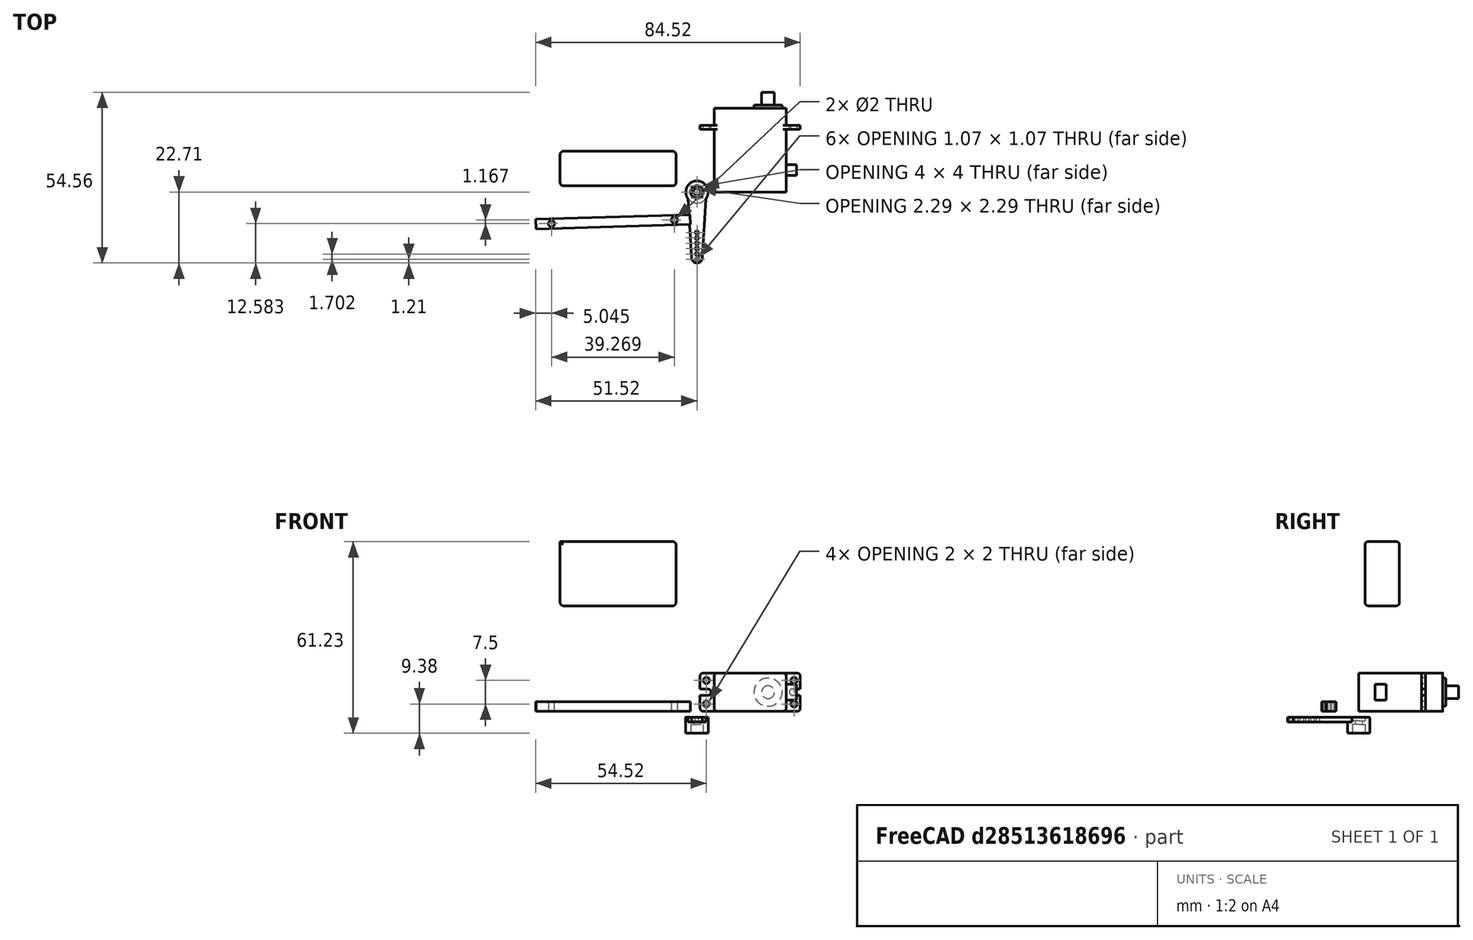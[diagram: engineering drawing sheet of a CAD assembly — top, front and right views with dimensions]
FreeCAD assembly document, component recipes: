
FREECAD ASSEMBLY — COMPONENT RECIPES ("ServoMount")

This assembly document has 3 components, labeled P0..P2 below (a component is one placed body or linked part). 1 of them carries a construction recipe — the FreeCAD feature program that regenerates the part from scratch, quoted from this document or its linked companion documents; the rest are supplied as boundary geometry only. No exploded tour is included for this assembly.
COMPONENT P0 — recipe-attached ("arm", modeled in this document).
Construction recipe (the document's own serialized feature program — sketch geometry with constraints, then the solid features built on it; lengths are millimeters unless a unit is written):

FEATURE [Sketcher::SketchObject] Sketch
  FullyConstrained = false
  MapMode = 5
  Support = -> [XY_Plane003]
  sketch-geometry (8):
    g0: LineSegment StartX=-56.9257 StartY=-11.8541 StartZ=0 EndX=-57.0196 EndY=-8.6971 EndZ=0
    g1: LineSegment StartX=-57.0196 StartY=-8.6971 StartZ=0 EndX=-7.75492 EndY=-7.23288 EndZ=0
    g2: LineSegment StartX=-7.75492 StartY=-7.23288 StartZ=0 EndX=-7.66109 EndY=-10.3899 EndZ=0
    g3: LineSegment StartX=-7.66109 StartY=-10.3899 StartZ=0 EndX=-56.9257 EndY=-11.8541 EndZ=0
    g4: Circle CenterX=-51.9748 CenterY=-10.1271 CenterZ=0 NormalX=0 NormalY=0 NormalZ=1 AngleXU=0 Radius=1
    g5: Circle CenterX=-12.7058 CenterY=-8.95993 CenterZ=0 NormalX=0 NormalY=0 NormalZ=1 AngleXU=0 Radius=1
    g6: LineSegment StartX=-51.9279 StartY=-11.7056 StartZ=0 EndX=-52.0218 EndY=-8.54856 EndZ=0
    g7: LineSegment StartX=-12.6589 StartY=-10.5384 StartZ=0 EndX=-12.7527 EndY=-7.38142 EndZ=0
  constraints (19):
    c: Coincident(g0,g1)
    c: Coincident(g1,g2)
    c: Coincident(g2,g3)
    c: Coincident(g3,g0)
    c: Perpendicular(g2,g3)
    c: Perpendicular(g1,g2)
    c: Perpendicular(g0,g3)
    c: PointOnObject(g6,g3)
    c: PointOnObject(g6,g1)
    c: Symmetric(g6,g6,g4)
    c: Perpendicular(g3,g6)
    c: Distance(g4,g0) = 5
    c: PointOnObject(g7,g3)
    c: PointOnObject(g7,g1)
    c: Perpendicular(g3,g7)
    c: Distance(g7,g2) = 5
    c: Symmetric(g7,g7,g5)
    c: Equal(g5,g4)
    c: Diameter(g5) = 2
FEATURE [PartDesign::Pad] Pad
  Direction = (0,0,1)
  Length = 3
  Length2 = 10
  Profile = -> Sketch
  ReferenceAxis = -> Sketch [N_Axis]
  Type = 0
FEATURE [PartDesign::CoordinateSystem] LCS_2
  AttacherType = Attacher::AttachEngine3D
  Support = -> [Pad]
FEATURE [PartDesign::Line] HoleAxis_1
  AttacherType = Attacher::AttachEngineLine
  Length = 6.29438
  MapMode = 19
  Placement = pos=(-12.7058,-8.95993,0) rot=(0,0,1;0rad)
  ResizeMode = 1
  Support = -> [Pad]
FEATURE [PartDesign::Line] HoleAxis_2
  AttacherType = Attacher::AttachEngineLine
  Length = 6.6495
  MapMode = 19
  Placement = pos=(-51.9748,-10.1271,0) rot=(0,0,1;0rad)
  ResizeMode = 1
  Support = -> [Pad]
FEATURE [PartDesign::Body] Body  label="arm"
  Group = -> [Sketch,Pad,LCS_2,HoleAxis_1,HoleAxis_2]
  Origin = -> Origin003
  Tip = -> Pad
COMPONENT P1 — geometry summary ("servo_part"; no construction recipe available for this part):
  bounding box: 32.0 x 31.9 x 12.2 mm
  tessellated surface: 488 triangles
  volume: 122599643269271110618356539178653623103013279177090359284854591830651926145662792439267340524648902817497553520130459448136483772809917173434393324192530432 mm^3 (985984215501790987695196999978682784905621967237516809497021927253952960936019258801087660708084060609000731809263823051364562005362390026564371558170624% of its bounding box)
  symmetry: mirror-symmetric across its z mid-plane
COMPONENT P2 — geometry summary ("servo_arm"; no construction recipe available for this part):
  bounding box: 25.6 x 7.1 x 5.2 mm
  tessellated surface: 296 triangles
  volume: 137600000000000004053199953239664631327328156390465222300101632684664201906804356746141460802389934080 mm^3 (14611903447154014275891121220549323014798439188025759577041575079126067034085274480678574277703761920% of its bounding box)
PROVENANCE & LICENSES
A FreeCAD (.FCStd) document from a public repository crawl; recipes are the document's own serialized feature recipes (and, for linked parts, companion documents' recipes).
License: as declared in the source repository (recorded in the dataset sidecar).
